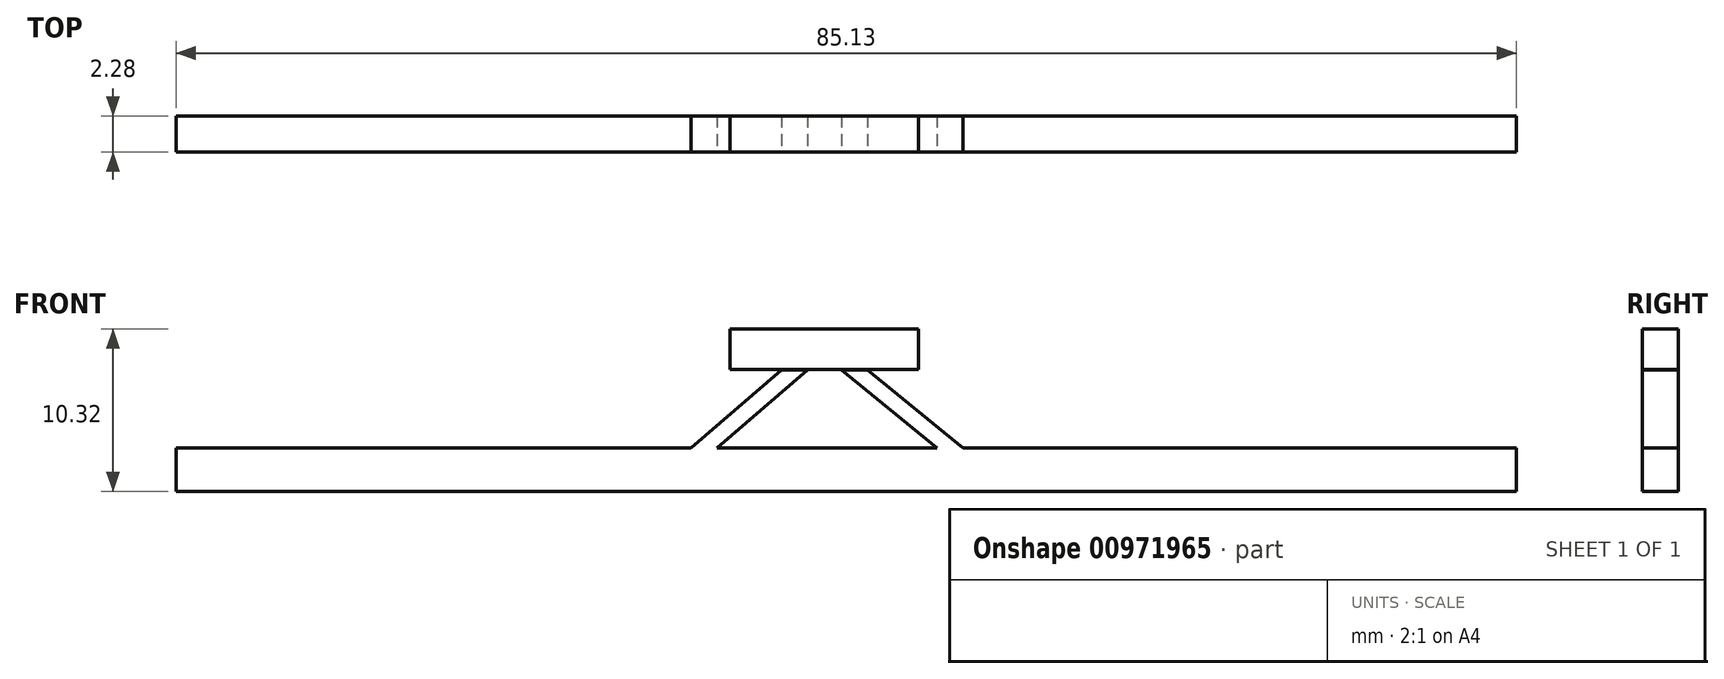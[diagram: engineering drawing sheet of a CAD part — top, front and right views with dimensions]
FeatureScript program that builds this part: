
annotation { "Feature Type Name" : "Feature", "Feature Type Description" : "" }
export const myFeature = defineFeature(function(context is Context, id is Id, definition is map)
    precondition{}
    {
        {
            var Q0;
            Q0=qCreatedBy(makeId("Front.planeOp"),FACE);
            var sketch = newSketch(context, id + "F0", { "sketchPlane" : qUnion([Q0])});
            skLineSegment(sketch, "E0.bottom", {"start": v(-42.7, 13.72) * mm, "end": v(42.42, 13.72) * mm});
            skLineSegment(sketch, "E0.top", {"start": v(-42.7, 16.5) * mm, "end": v(42.42, 16.5) * mm});
            skLineSegment(sketch, "E0.left", {"start": v(-42.7, 13.72) * mm, "end": v(-42.7, 16.5) * mm});
            skLineSegment(sketch, "E0.right", {"start": v(42.42, 13.72) * mm, "end": v(42.42, 16.5) * mm});
            skPoint(sketch, "E1.endSnap0", {"position": v(-0.14, 13.72) * mm});
            skLineSegment(sketch, "E2", {"start": v(-8.6, 16.5) * mm, "end": v(14.6, 16.5) * mm});
            skLineSegment(sketch, "E3", {"start": v(-10.01, 16.5) * mm, "end": v(-8.6, 16.5) * mm});
            skLineSegment(sketch, "E4", {"start": v(14.6, 16.5) * mm, "end": v(16.02, 16.5) * mm});
            skLineSegment(sketch, "E5.top", {"start": v(5.63, 13.72) * mm, "end": v(-8.36, 13.72) * mm});
            skLineSegment(sketch, "E6", {"start": v(1.2, 8.77) * mm, "end": v(-0.45, 8.77) * mm});
            skLineSegment(sketch, "E7", {"start": v(-2.6, 8.77) * mm, "end": v(-4.24, 8.77) * mm});
            skPoint(sketch, "E8", {"position": v(7.28, 13.72) * mm});
            skPoint(sketch, "E9", {"position": v(-10.01, 13.72) * mm});
            skLineSegment(sketch, "E10", {"start": v(1.2, 8.77) * mm, "end": v(7.28, 13.72) * mm});
            skLineSegment(sketch, "E11", {"start": v(7.28, 13.72) * mm, "end": v(5.63, 13.72) * mm});
            skLineSegment(sketch, "E12", {"start": v(5.63, 13.72) * mm, "end": v(-0.45, 8.77) * mm});
            skLineSegment(sketch, "E13", {"start": v(-0.45, 8.77) * mm, "end": v(1.2, 8.77) * mm});
            skLineSegment(sketch, "E14", {"start": v(-8.36, 13.72) * mm, "end": v(-2.6, 8.77) * mm});
            skLineSegment(sketch, "E15", {"start": v(-10.01, 13.72) * mm, "end": v(-4.24, 8.77) * mm});
            skLineSegment(sketch, "E16", {"start": v(-8.36, 13.72) * mm, "end": v(-10.01, 13.72) * mm});
            skLineSegment(sketch, "E17", {"start": v(-0.45, 8.77) * mm, "end": v(-2.6, 8.77) * mm});
            skLineSegment(sketch, "E18", {"start": v(1.2, 8.77) * mm, "end": v(-4.24, 8.77) * mm});
            skLineSegment(sketch, "E19", {"start": v(-1.52, 8.77) * mm, "end": v(-1.52, 0.7) * mm});
            skPoint(sketch, "E20.middle", {"position": v(-1.52, 6.81) * mm});
            skLineSegment(sketch, "E21.bottom", {"start": v(4.46, 6.18) * mm, "end": v(-7.5, 6.18) * mm});
            skLineSegment(sketch, "E21.top", {"start": v(4.46, 8.76) * mm, "end": v(-7.5, 8.76) * mm});
            skLineSegment(sketch, "E21.left", {"start": v(4.46, 6.18) * mm, "end": v(4.46, 7.47) * mm});
            skLineSegment(sketch, "E21.right", {"start": v(-7.5, 6.18) * mm, "end": v(-7.5, 7.47) * mm});
            skPoint(sketch, "E21.middle", {"position": v(-1.52, 7.47) * mm});
            skLineSegment(sketch, "E22", {"start": v(-7.5, 7.47) * mm, "end": v(-10.05, 7.47) * mm});
            skLineSegment(sketch, "E23", {"start": v(4.46, 7.47) * mm, "end": v(7, 7.47) * mm});
            skLineSegment(sketch, "E24", {"start": v(-7.5, 7.47) * mm, "end": v(-7.5, 8.76) * mm});
            skLineSegment(sketch, "E25", {"start": v(4.46, 7.47) * mm, "end": v(4.46, 8.76) * mm});
            skLineSegment(sketch, "E26.bottom", {"start": v(-7.5, 8.12) * mm, "end": v(-10.05, 8.12) * mm});
            skLineSegment(sketch, "E26.left", {"start": v(-7.5, 8.12) * mm, "end": v(-7.5, 7.47) * mm});
            skLineSegment(sketch, "E26.right", {"start": v(-10.05, 8.12) * mm, "end": v(-10.05, 7.47) * mm});
            skLineSegment(sketch, "E27.bottom", {"start": v(-7.5, 6.83) * mm, "end": v(-10.05, 6.83) * mm});
            skLineSegment(sketch, "E27.left", {"start": v(-7.5, 6.83) * mm, "end": v(-7.5, 7.47) * mm});
            skLineSegment(sketch, "E27.right", {"start": v(-10.05, 6.83) * mm, "end": v(-10.05, 7.47) * mm});
            skLineSegment(sketch, "E28.bottom", {"start": v(4.46, 8.12) * mm, "end": v(7, 8.12) * mm});
            skLineSegment(sketch, "E28.left", {"start": v(4.46, 8.12) * mm, "end": v(4.46, 7.47) * mm});
            skLineSegment(sketch, "E28.right", {"start": v(7, 8.12) * mm, "end": v(7, 7.47) * mm});
            skLineSegment(sketch, "E29.bottom", {"start": v(4.46, 6.83) * mm, "end": v(7, 6.83) * mm});
            skLineSegment(sketch, "E29.left", {"start": v(4.46, 6.83) * mm, "end": v(4.46, 7.47) * mm});
            skLineSegment(sketch, "E29.right", {"start": v(7, 6.83) * mm, "end": v(7, 7.47) * mm});
            skSolve(sketch);
        }
        {
            var Q0;
            {var subQ4=sQuery(id+"F0.wireOp",EDGE,"E0.left");Q0=makeQuery(id+"F0.imprint","IMPRINT",FACE,{"disambiguationData":[TD([[makeQuery(id+"F0.imprint","IMPRINT",EDGE,{"derivedFrom":subQ4}),-1.0]])]});}
            var Q1;
            {var subQ0=sQuery(id+"F0.wireOp",EDGE,"E10");Q1=makeQuery(id+"F0.imprint","IMPRINT",FACE,{"disambiguationData":[TD([[makeQuery(id+"F0.imprint","IMPRINT",EDGE,{"derivedFrom":subQ0}),1.0]])]});}
            var Q2;
            {var subQ0=sQuery(id+"F0.wireOp",EDGE,"E14");Q2=makeQuery(id+"F0.imprint","IMPRINT",FACE,{"disambiguationData":[TD([[makeQuery(id+"F0.imprint","IMPRINT",EDGE,{"derivedFrom":subQ0}),-1.0]])]});}
            var Q3;
            {var subQ5=sQuery(id+"F0.wireOp",EDGE,"E21.right");Q3=makeQuery(id+"F0.imprint","IMPRINT",FACE,{"disambiguationData":[TD([[makeQuery(id+"F0.imprint","IMPRINT",EDGE,{"derivedFrom":subQ5}),-1.0]])]});}
            var Q4;
            {var subQ5=sQuery(id+"F0.wireOp",EDGE,"E21.left");Q4=makeQuery(id+"F0.imprint","IMPRINT",FACE,{"disambiguationData":[TD([[makeQuery(id+"F0.imprint","IMPRINT",EDGE,{"derivedFrom":subQ5}),1.0]])]});}
            extrude(context, id + "F1", {"entities" : qUnion([Q0, Q1, Q2, Q3, Q4]), "depth" : 2.3 * mm, "offsetDistance" : 25.4 * mm});
        }
        {
            var Q0;
            Q0=makeQuery(id+"F1.opExtrude","SWEPT_BODY",BODY,{"disambiguationData":[OSD([sQuery(id+"F0.wireOp",EDGE,"E0.bottom"),sQuery(id+"F0.wireOp",EDGE,"E0.top"),sQuery(id+"F0.wireOp",EDGE,"E0.left"),sQuery(id+"F0.wireOp",EDGE,"E0.right"),sQuery(id+"F0.wireOp",EDGE,"E2"),sQuery(id+"F0.wireOp",EDGE,"E4"),sQuery(id+"F0.wireOp",EDGE,"E3"),sQuery(id+"F0.wireOp",EDGE,"E10"),sQuery(id+"F0.wireOp",EDGE,"E12"),sQuery(id+"F0.wireOp",EDGE,"E14"),sQuery(id+"F0.wireOp",EDGE,"E15"),sQuery(id+"F0.wireOp",EDGE,"E5.top"),sQuery(id+"F0.wireOp",EDGE,"E18")])]});
            var Q1;
            Q1=makeQuery(id+"F1.opExtrude","SWEPT_BODY",BODY,{"disambiguationData":[OSD([sQuery(id+"F0.wireOp",EDGE,"E21.bottom"),sQuery(id+"F0.wireOp",EDGE,"E21.top"),sQuery(id+"F0.wireOp",EDGE,"E21.left"),sQuery(id+"F0.wireOp",EDGE,"E21.right")])]});
            var Q2;
            Q2=makeQuery(id+"F1.opExtrude","CAP_EDGE",EDGE,{"disambiguationData":[OSD([sQuery(id+"F0.wireOp",EDGE,"E21.top")])],"isStart":false});
            transform(context, id + "F2", {"entities" : qUnion([Q0, Q1]), "transformType" : TransformType.ROTATION, "transformAxis" : qUnion([Q2]), "angle" : 180 * degree, "makeCopy" : false});
        }
    });
